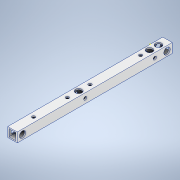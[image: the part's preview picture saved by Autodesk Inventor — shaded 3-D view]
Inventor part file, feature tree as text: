
AUTODESK INVENTOR PART (.ipt)
format: ipt  version: 2020.3 (Build 243373000, 373)  size: 207,360 bytes
history: native  units: mm
features: sketch x11, hole x7, extrude x3, other x1
ambient origin geometry x8: Origin, YZ Plane, XZ Plane, XY Plane, X Axis, Y Axis, Z Axis, Center Point
bodies: Body1 (feature_tree)
feature tree (22):
  other  "ソリッド1"
  extrude  "押し出し1"  Depth=9.0mm
  hole  "穴1"  [1 undecoded]
  hole  "穴2"  [1 undecoded]
  extrude  "押し出し3"  Depth=6.6mm
  hole  "穴4"  [1 undecoded]
  extrude  "押し出し4"  Depth=1.2mm
  hole  "穴5"  [1 undecoded]
  hole  "穴6"  [1 undecoded]
  sketch  "スケッチ11"
  hole  "穴7"  [1 undecoded]
  hole  "穴8"  [1 undecoded]
  sketch  "スケッチ1"
  sketch  "スケッチ2"
  sketch  "スケッチ3"
  sketch  "スケッチ6"
  sketch  "スケッチ7"
  sketch  "スケッチ8"
  sketch  "スケッチ9"
  sketch  "スケッチ10"
  sketch  "スケッチ12"
  sketch  "スケッチ13"
note: 7 required parameter values undecoded (feature->parameter linkage not recoverable at this tier; creation-order binding heuristic only, values carry confidence <= 0.55)
